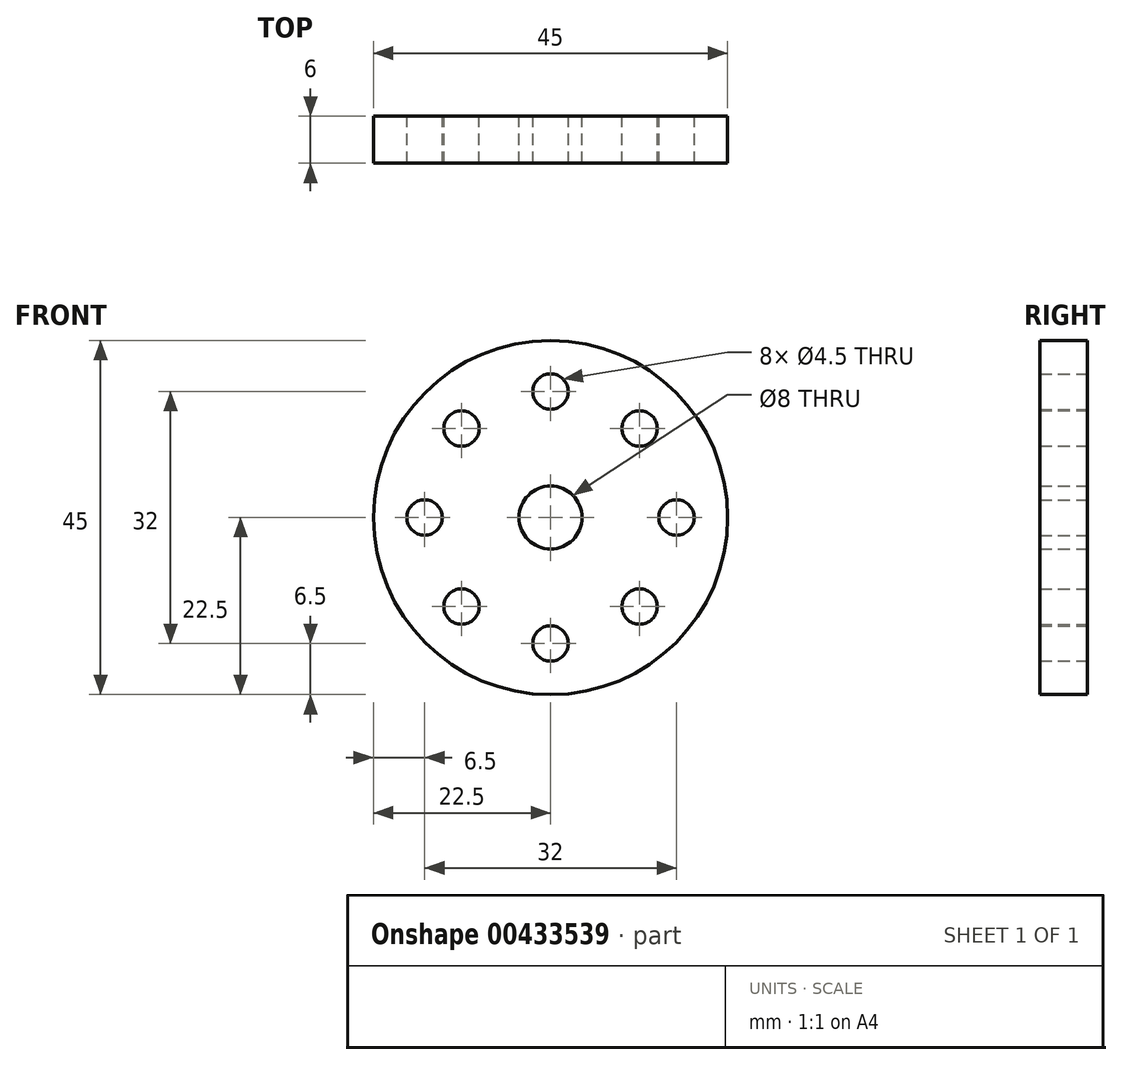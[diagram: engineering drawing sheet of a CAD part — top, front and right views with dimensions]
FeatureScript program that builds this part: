
annotation { "Feature Type Name" : "Feature", "Feature Type Description" : "" }
export const myFeature = defineFeature(function(context is Context, id is Id, definition is map)
    precondition{}
    {
        {
            var Q0;
            Q0=qCreatedBy(makeId("Front.planeOp"),FACE);
            var sketch = newSketch(context, id + "F0", { "sketchPlane" : qUnion([Q0])});
            skCircle(sketch, "E0", {"center": v(0, 0) * mm, "radius": 22.5 * mm});
            skCircle(sketch, "E1", {"center": v(0, 0) * mm, "radius": 16 * mm});
            skCircle(sketch, "E2", {"center": v(0, 16) * mm, "radius": 2.25 * mm});
            skCircle(sketch, "E3.1.0", {"center": v(-11.31, 11.31) * mm, "radius": 2.25 * mm});
            skCircle(sketch, "E3.2.0", {"center": v(-16, 0) * mm, "radius": 2.25 * mm});
            skCircle(sketch, "E3.3.0", {"center": v(-11.31, -11.31) * mm, "radius": 2.25 * mm});
            skCircle(sketch, "E3.4.0", {"center": v(0, -16) * mm, "radius": 2.25 * mm});
            skCircle(sketch, "E3.5.0", {"center": v(11.31, -11.31) * mm, "radius": 2.25 * mm});
            skCircle(sketch, "E3.6.0", {"center": v(16, 0) * mm, "radius": 2.25 * mm});
            skCircle(sketch, "E3.7.0", {"center": v(11.31, 11.31) * mm, "radius": 2.25 * mm});
            skCircle(sketch, "E4", {"center": v(0, 0) * mm, "radius": 4 * mm});
            skSolve(sketch);
        }
        {
            var Q0;
            Q0 = qSketchRegion(id + "F0", true);
            var Q1;
            Q1=makeQuery(id+"F0.imprint","IMPRINT",FACE,{"disambiguationData":[TD([[makeQuery(id+"F0.imprint","IMPRINT",EDGE,{"derivedFrom":sQuery(id+"F0.wireOp",EDGE,"E4")}),-1.0]])]});
            extrude(context, id + "F1", {"entities" : qUnion([Q0, Q1]), "depth" : 6 * mm});
        }
    });
